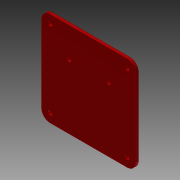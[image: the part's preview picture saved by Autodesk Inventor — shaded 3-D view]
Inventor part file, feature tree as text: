
AUTODESK INVENTOR PART (.ipt)
format: ipt  version: 2015 (Build 190159000, 159)  size: 104,960 bytes
history: native  units: in
note: dims shown in document units (in); Inventor stores cm internally (conversion verified against a paired STEP export)
features: sketch x3, extrude x2, hole x1
ambient origin geometry x8: Origin, YZ Plane, XZ Plane, XY Plane, X Axis, Y Axis, Z Axis, Center Point
bodies: Solid1 (feature_tree)
feature tree (6):
  extrude  "Extrusion1"  Depth=2.75in
  hole  "Hole1"  [1 undecoded]
  extrude  "Extrusion2"  Depth=0.25in
  sketch  "Sketch1"  dims[d0=2.75in d1=2.75in]
  sketch  "Sketch2"  dims[d2=0.25in d3=0.08in d4=0.0in]
  sketch  "Sketch3"  dims[d5=0.126in d6=0.75in d7=0.2205in d8=0.25in d9=90.0deg d10=1.0in d11=0.8108in d12=0.126in d13=1.15in d14=0.5in d16=0.15in d17=0.0in d22=0.126in]
note: 1 required parameter value undecoded (feature->parameter linkage not recoverable at this tier; creation-order binding heuristic only, values carry confidence <= 0.55)
